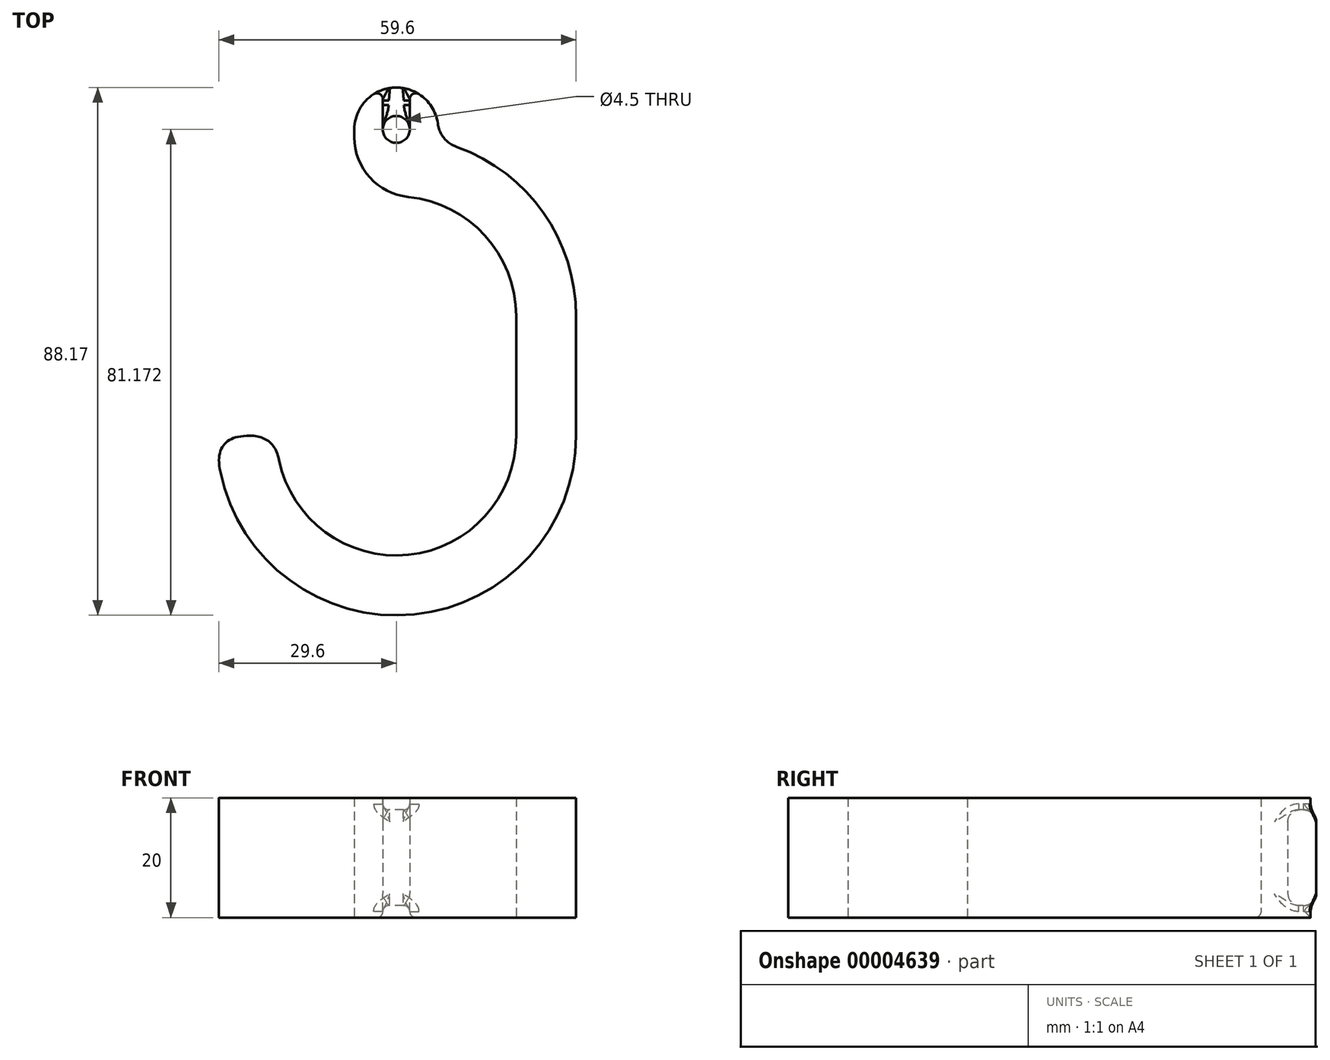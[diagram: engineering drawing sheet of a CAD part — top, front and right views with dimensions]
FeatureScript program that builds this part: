
annotation { "Feature Type Name" : "Feature", "Feature Type Description" : "" }
export const myFeature = defineFeature(function(context is Context, id is Id, definition is map)
    precondition{}
    {
        {
            var Q0;
            Q0=qCreatedBy(makeId("Top.planeOp"),FACE);
            var sketch = newSketch(context, id + "F0", { "sketchPlane" : qUnion([Q0])});
            skArc(sketch, "E0", {"start": v(-20, 0) * mm, "mid": v(0, -20) * mm, "end": v(20, 0) * mm});
            skArc(sketch, "E1", {"start": v(-30, 0) * mm, "mid": v(0, -30) * mm, "end": v(30, 0) * mm});
            skLineSegment(sketch, "E2", {"start": v(30, 0) * mm, "end": v(30, 20) * mm});
            skLineSegment(sketch, "E3", {"start": v(20, 0) * mm, "end": v(20, 20) * mm});
            skArc(sketch, "E4", {"start": v(30, 20) * mm, "mid": v(23.56, 38.57) * mm, "end": v(7, 49.17) * mm});
            skLineSegment(sketch, "E5", {"start": v(-20, 0) * mm, "end": v(-30, 0) * mm});
            skLineSegment(sketch, "E6", {"start": v(-7, 51.17) * mm, "end": v(-7, 40) * mm});
            skLineSegment(sketch, "E7", {"start": v(-7, 40) * mm, "end": v(0, 40) * mm});
            skArc(sketch, "E8", {"start": v(20, 20) * mm, "mid": v(14.14, 34.14) * mm, "end": v(0, 40) * mm});
            skPoint(sketch, "E9.center.orphan", {"position": v(0, 49.17) * mm});
            skLineSegment(sketch, "E10", {"start": v(7, 49.17) * mm, "end": v(7, 51.17) * mm});
            skArc(sketch, "E11", {"start": v(-7, 51.17) * mm, "mid": v(0, 58.17) * mm, "end": v(7, 51.17) * mm});
            skCircle(sketch, "E12", {"center": v(0, 51.17) * mm, "radius": 2.25 * mm});
            skSolve(sketch);
        }
        {
            var Q0;
            Q0 = qSketchRegion(id + "F0", true);
            extrude(context, id + "F1", {"entities" : qUnion([Q0]), "endBound" : BoundingType.SYMMETRIC, "depth" : 20 * mm});
        }
        {
            var Q0;
            Q0=makeQuery(id+"F1.opExtrude","SWEPT_EDGE",EDGE,{"disambiguationData":[OSD([sQuery(id+"F0.wireOp",EDGE,"E1"),sQuery(id+"F0.wireOp",EDGE,"E5")])]});
            var Q1;
            Q1=makeQuery(id+"F1.opExtrude","SWEPT_EDGE",EDGE,{"disambiguationData":[OSD([sQuery(id+"F0.wireOp",EDGE,"E0"),sQuery(id+"F0.wireOp",EDGE,"E5")])]});
            var Q2;
            Q2=makeQuery(id+"F1.opExtrude","SWEPT_EDGE",EDGE,{"disambiguationData":[OSD([sQuery(id+"F0.wireOp",EDGE,"E4"),sQuery(id+"F0.wireOp",EDGE,"E10")])]});
            fillet(context, id + "F2", {"entities" : qUnion([Q0, Q1, Q2]), "radius" : 5 * mm, "tangentPropagation" : true, "rho" : 0.5, "crossSection" : FilletCrossSection.CONIC, "allowEdgeOverflow" : false});
        }
        {
            var Q0;
            Q0=makeQuery(id+"F1.opExtrude","SWEPT_EDGE",EDGE,{"disambiguationData":[OSD([sQuery(id+"F0.wireOp",EDGE,"E6"),sQuery(id+"F0.wireOp",EDGE,"E7")])]});
            fillet(context, id + "F3", {"entities" : qUnion([Q0]), "radius" : 10 * mm, "tangentPropagation" : true, "allowEdgeOverflow" : false});
        }
        {
            var Q0;
            Q0=qCreatedBy(makeId("Right.planeOp"),FACE);
            var sketch = newSketch(context, id + "F4", { "sketchPlane" : qUnion([Q0])});
            skLineSegment(sketch, "E13.bottom", {"start": v(58.17, 10) * mm, "end": v(51.17, 10) * mm});
            skLineSegment(sketch, "E13.top", {"start": v(58.17, 8) * mm, "end": v(51.17, 8) * mm});
            skLineSegment(sketch, "E13.left", {"start": v(58.17, 10) * mm, "end": v(58.17, 8) * mm});
            skLineSegment(sketch, "E13.right", {"start": v(51.17, 10) * mm, "end": v(51.17, 8) * mm});
            skLineSegment(sketch, "E14.bottom", {"start": v(58.17, -10) * mm, "end": v(51.17, -10) * mm});
            skLineSegment(sketch, "E14.top", {"start": v(58.17, -8) * mm, "end": v(51.17, -8) * mm});
            skLineSegment(sketch, "E14.left", {"start": v(58.17, -10) * mm, "end": v(58.17, -8) * mm});
            skLineSegment(sketch, "E14.right", {"start": v(51.17, -10) * mm, "end": v(51.17, -8) * mm});
            skLineSegment(sketch, "E15.0", {"start": v(48.92, -10) * mm, "end": v(53.42, -10) * mm, "construction": true});
            skLineSegment(sketch, "E16.0", {"start": v(48.92, 10) * mm, "end": v(53.42, 10) * mm, "construction": true});
            skLineSegment(sketch, "E17.0", {"start": v(58.17, 10) * mm, "end": v(51.17, 10) * mm, "construction": true});
            skLineSegment(sketch, "E18.0", {"start": v(58.17, -10) * mm, "end": v(51.17, -10) * mm, "construction": true});
            skSolve(sketch);
        }
        {
            var Q0;
            Q0 = qSketchRegion(id + "F4", true);
            extrude(context, id + "F5", {"entities" : qUnion([Q0]), "operationType" : NewBodyOperationType.REMOVE, "endBound" : BoundingType.SYMMETRIC, "oppositeDirection" : true, "depth" : 4.5 * mm});
        }
        {
            var Q0;
            Q0=makeQuery(id+"F5.boolean.opBoolean","INTERSECT",EDGE,{"derivedFrom":[makeQuery(id+"F1.opExtrude","SWEPT_FACE",FACE,{"disambiguationData":[OSD([sQuery(id+"F0.wireOp",EDGE,"E11")])]}),makeQuery(id+"F5.opExtrude","SWEPT_FACE",FACE,{"disambiguationData":[OSD([sQuery(id+"F4.wireOp",EDGE,"E14.top")])]})]});
            var Q1;
            Q1=makeQuery(id+"F5.boolean.opBoolean","INTERSECT",EDGE,{"derivedFrom":[makeQuery(id+"F1.opExtrude","SWEPT_FACE",FACE,{"disambiguationData":[OSD([sQuery(id+"F0.wireOp",EDGE,"E12")])]}),makeQuery(id+"F5.opExtrude","SWEPT_FACE",FACE,{"disambiguationData":[OSD([sQuery(id+"F4.wireOp",EDGE,"E14.top")])]})]});
            var Q2;
            Q2=makeQuery(id+"F5.boolean.opBoolean","INTERSECT",EDGE,{"derivedFrom":[makeQuery(id+"F1.opExtrude","SWEPT_FACE",FACE,{"disambiguationData":[OSD([sQuery(id+"F0.wireOp",EDGE,"E11")])]}),makeQuery(id+"F5.opExtrude","SWEPT_FACE",FACE,{"disambiguationData":[OSD([sQuery(id+"F4.wireOp",EDGE,"E13.top")])]})]});
            var Q3;
            Q3=makeQuery(id+"F5.boolean.opBoolean","INTERSECT",EDGE,{"derivedFrom":[makeQuery(id+"F1.opExtrude","SWEPT_FACE",FACE,{"disambiguationData":[OSD([sQuery(id+"F0.wireOp",EDGE,"E12")])]}),makeQuery(id+"F5.opExtrude","SWEPT_FACE",FACE,{"disambiguationData":[OSD([sQuery(id+"F4.wireOp",EDGE,"E13.top")])]})]});
            fillet(context, id + "F6", {"entities" : qUnion([Q0, Q1, Q2, Q3]), "radius" : 2 * mm, "tangentPropagation" : true, "allowEdgeOverflow" : false});
        }
        {
            var Q0;
            Q0=makeQuery(id+"F5.boolean.opBoolean","INTERSECT",EDGE,{"derivedFrom":[makeQuery(id+"F1.opExtrude","SWEPT_FACE",FACE,{"disambiguationData":[OSD([sQuery(id+"F0.wireOp",EDGE,"E11")])]}),makeQuery(id+"F5.opExtrude","CAP_FACE",FACE,{"disambiguationData":[OSD([sQuery(id+"F4.wireOp",EDGE,"E13.bottom"),sQuery(id+"F4.wireOp",EDGE,"E13.top"),sQuery(id+"F4.wireOp",EDGE,"E13.left"),sQuery(id+"F4.wireOp",EDGE,"E13.right")])],"isStart":false})]});
            var Q1;
            Q1=makeQuery(id+"F5.boolean.opBoolean","INTERSECT",EDGE,{"derivedFrom":[makeQuery(id+"F1.opExtrude","SWEPT_FACE",FACE,{"disambiguationData":[OSD([sQuery(id+"F0.wireOp",EDGE,"E11")])]}),makeQuery(id+"F5.opExtrude","CAP_FACE",FACE,{"disambiguationData":[OSD([sQuery(id+"F4.wireOp",EDGE,"E13.bottom"),sQuery(id+"F4.wireOp",EDGE,"E13.top"),sQuery(id+"F4.wireOp",EDGE,"E13.left"),sQuery(id+"F4.wireOp",EDGE,"E13.right")])],"isStart":true})]});
            var Q2;
            Q2=makeQuery(id+"F5.boolean.opBoolean","INTERSECT",EDGE,{"derivedFrom":[makeQuery(id+"F1.opExtrude","SWEPT_FACE",FACE,{"disambiguationData":[OSD([sQuery(id+"F0.wireOp",EDGE,"E11")])]}),makeQuery(id+"F5.opExtrude","CAP_FACE",FACE,{"disambiguationData":[OSD([sQuery(id+"F4.wireOp",EDGE,"E14.bottom"),sQuery(id+"F4.wireOp",EDGE,"E14.top"),sQuery(id+"F4.wireOp",EDGE,"E14.left"),sQuery(id+"F4.wireOp",EDGE,"E14.right")])],"isStart":false})]});
            var Q3;
            Q3=makeQuery(id+"F5.boolean.opBoolean","INTERSECT",EDGE,{"derivedFrom":[makeQuery(id+"F1.opExtrude","SWEPT_FACE",FACE,{"disambiguationData":[OSD([sQuery(id+"F0.wireOp",EDGE,"E11")])]}),makeQuery(id+"F5.opExtrude","CAP_FACE",FACE,{"disambiguationData":[OSD([sQuery(id+"F4.wireOp",EDGE,"E14.bottom"),sQuery(id+"F4.wireOp",EDGE,"E14.top"),sQuery(id+"F4.wireOp",EDGE,"E14.left"),sQuery(id+"F4.wireOp",EDGE,"E14.right")])],"isStart":true})]});
            var Q4;
            {var subQ0=sQuery(id+"F4.wireOp",EDGE,"E14.top");Q4=makeQuery(id+"F6.opFillet","BLEND_EDGE",EDGE,{"blendedFrom":[makeQuery(id+"F5.boolean.opBoolean","INTERSECT",EDGE,{"derivedFrom":[makeQuery(id+"F1.opExtrude","SWEPT_FACE",FACE,{"disambiguationData":[OSD([sQuery(id+"F0.wireOp",EDGE,"E12")])]}),makeQuery(id+"F5.opExtrude","SWEPT_FACE",FACE,{"disambiguationData":[OSD([subQ0])]})]}),makeQuery(id+"F5.boolean.opBoolean","COPY",FACE,{"derivedFrom":makeQuery(id+"F5.opExtrude","CAP_FACE",FACE,{"disambiguationData":[OSD([sQuery(id+"F4.wireOp",EDGE,"E14.bottom"),subQ0,sQuery(id+"F4.wireOp",EDGE,"E14.left"),sQuery(id+"F4.wireOp",EDGE,"E14.right")])],"isStart":true})})],"blendedInto":[makeQuery(id+"F5.boolean.opBoolean","COPY",FACE,{"derivedFrom":makeQuery(id+"F5.opExtrude","CAP_FACE",FACE,{"disambiguationData":[OSD([sQuery(id+"F4.wireOp",EDGE,"E14.bottom"),subQ0,sQuery(id+"F4.wireOp",EDGE,"E14.left"),sQuery(id+"F4.wireOp",EDGE,"E14.right")])],"isStart":true})})]});}
            var Q5;
            Q5=makeQuery(id+"F5.boolean.opBoolean","COPY",FACE,{"derivedFrom":makeQuery(id+"F5.opExtrude","CAP_FACE",FACE,{"disambiguationData":[OSD([sQuery(id+"F4.wireOp",EDGE,"E14.bottom"),sQuery(id+"F4.wireOp",EDGE,"E14.top"),sQuery(id+"F4.wireOp",EDGE,"E14.left"),sQuery(id+"F4.wireOp",EDGE,"E14.right")])],"isStart":false})});
            var Q6;
            {var subQ0=sQuery(id+"F4.wireOp",EDGE,"E13.top");Q6=makeQuery(id+"F6.opFillet","BLEND_EDGE",EDGE,{"blendedFrom":[makeQuery(id+"F5.boolean.opBoolean","INTERSECT",EDGE,{"derivedFrom":[makeQuery(id+"F1.opExtrude","SWEPT_FACE",FACE,{"disambiguationData":[OSD([sQuery(id+"F0.wireOp",EDGE,"E12")])]}),makeQuery(id+"F5.opExtrude","SWEPT_FACE",FACE,{"disambiguationData":[OSD([subQ0])]})]}),makeQuery(id+"F5.boolean.opBoolean","COPY",FACE,{"derivedFrom":makeQuery(id+"F5.opExtrude","CAP_FACE",FACE,{"disambiguationData":[OSD([sQuery(id+"F4.wireOp",EDGE,"E13.bottom"),subQ0,sQuery(id+"F4.wireOp",EDGE,"E13.left"),sQuery(id+"F4.wireOp",EDGE,"E13.right")])],"isStart":true})})],"blendedInto":[makeQuery(id+"F5.boolean.opBoolean","COPY",FACE,{"derivedFrom":makeQuery(id+"F5.opExtrude","CAP_FACE",FACE,{"disambiguationData":[OSD([sQuery(id+"F4.wireOp",EDGE,"E13.bottom"),subQ0,sQuery(id+"F4.wireOp",EDGE,"E13.left"),sQuery(id+"F4.wireOp",EDGE,"E13.right")])],"isStart":true})})]});}
            var Q7;
            {var subQ0=sQuery(id+"F4.wireOp",EDGE,"E13.top");Q7=makeQuery(id+"F6.opFillet","BLEND_EDGE",EDGE,{"blendedFrom":[makeQuery(id+"F5.boolean.opBoolean","INTERSECT",EDGE,{"derivedFrom":[makeQuery(id+"F1.opExtrude","SWEPT_FACE",FACE,{"disambiguationData":[OSD([sQuery(id+"F0.wireOp",EDGE,"E12")])]}),makeQuery(id+"F5.opExtrude","SWEPT_FACE",FACE,{"disambiguationData":[OSD([subQ0])]})]}),makeQuery(id+"F5.boolean.opBoolean","COPY",FACE,{"derivedFrom":makeQuery(id+"F5.opExtrude","CAP_FACE",FACE,{"disambiguationData":[OSD([sQuery(id+"F4.wireOp",EDGE,"E13.bottom"),subQ0,sQuery(id+"F4.wireOp",EDGE,"E13.left"),sQuery(id+"F4.wireOp",EDGE,"E13.right")])],"isStart":false})})],"blendedInto":[makeQuery(id+"F5.boolean.opBoolean","COPY",FACE,{"derivedFrom":makeQuery(id+"F5.opExtrude","CAP_FACE",FACE,{"disambiguationData":[OSD([sQuery(id+"F4.wireOp",EDGE,"E13.bottom"),subQ0,sQuery(id+"F4.wireOp",EDGE,"E13.left"),sQuery(id+"F4.wireOp",EDGE,"E13.right")])],"isStart":false})})]});}
            var Q8;
            Q8=makeQuery(id+"F5.boolean.opBoolean","COPY",EDGE,{"derivedFrom":makeQuery(id+"F5.opExtrude","CAP_EDGE",EDGE,{"disambiguationData":[OSD([sQuery(id+"F4.wireOp",EDGE,"E13.bottom")])],"isStart":true})});
            fillet(context, id + "F7", {"entities" : qUnion([Q0, Q1, Q2, Q3, Q4, Q5, Q6, Q7, Q8]), "radius" : 1 * mm, "tangentPropagation" : true, "allowEdgeOverflow" : false});
        }
    });
